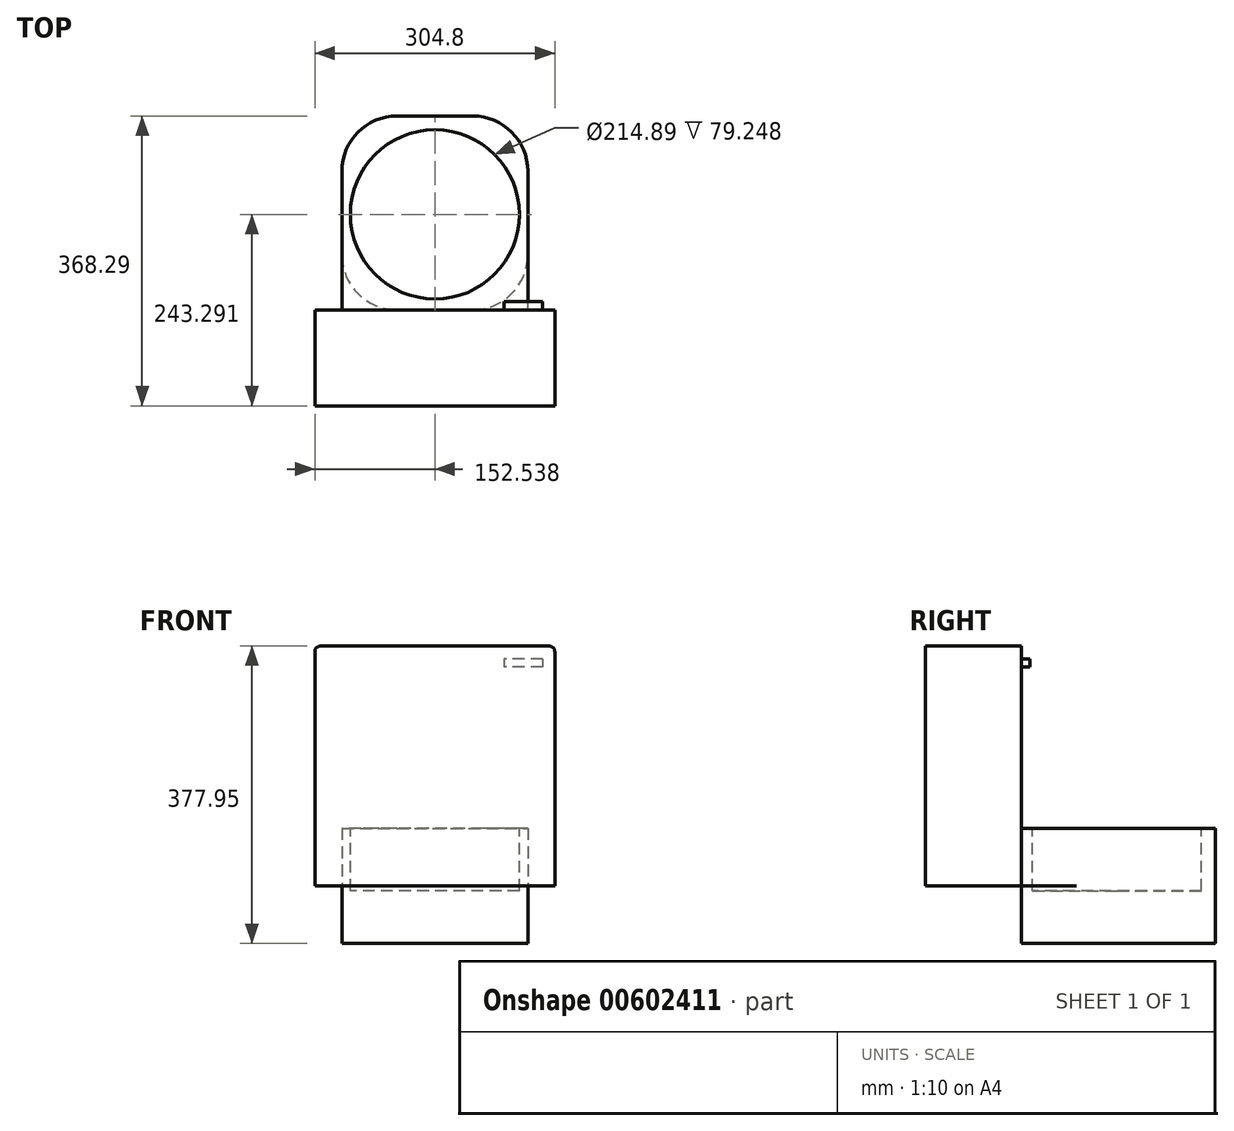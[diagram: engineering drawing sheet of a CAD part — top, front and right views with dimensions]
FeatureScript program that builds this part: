
annotation { "Feature Type Name" : "Feature", "Feature Type Description" : "" }
export const myFeature = defineFeature(function(context is Context, id is Id, definition is map)
    precondition{}
    {
        {
            var Q0;
            Q0=qCreatedBy(makeId("Top.planeOp"),FACE);
            var sketch = newSketch(context, id + "F0", { "sketchPlane" : qUnion([Q0])});
            skLineSegment(sketch, "E0.bottom", {"start": v(0, 0) * mm, "end": v(304.8, 0) * mm});
            skLineSegment(sketch, "E0.top", {"start": v(0, -121.92) * mm, "end": v(304.8, -121.92) * mm});
            skLineSegment(sketch, "E0.left", {"start": v(0, 0) * mm, "end": v(0, -121.92) * mm});
            skLineSegment(sketch, "E0.right", {"start": v(304.8, 0) * mm, "end": v(304.8, -121.92) * mm});
            skSolve(sketch);
        }
        {
            var Q0;
            Q0=makeQuery(id+"F0.imprint","IMPRINT",FACE,{"disambiguationData":[TD([[makeQuery(id+"F0.imprint","IMPRINT",EDGE,{"derivedFrom":sQuery(id+"F0.wireOp",EDGE,"E0.bottom")}),-1.0]])]});
            extrude(context, id + "F1", {"entities" : qUnion([Q0]), "depth" : 304.8 * mm, "offsetDistance" : 30.48 * mm});
        }
        {
            var Q0;
            Q0=qCreatedBy(makeId("Top.planeOp"),FACE);
            var sketch = newSketch(context, id + "F2", { "sketchPlane" : qUnion([Q0])});
            skLineSegment(sketch, "E1.bottom", {"start": v(34.53, 0) * mm, "end": v(270.55, 0) * mm});
            skLineSegment(sketch, "E1.top", {"start": v(34.53, 246.37) * mm, "end": v(270.55, 246.37) * mm});
            skLineSegment(sketch, "E1.left", {"start": v(34.53, 0) * mm, "end": v(34.53, 246.37) * mm});
            skLineSegment(sketch, "E1.right", {"start": v(270.55, 0) * mm, "end": v(270.55, 246.37) * mm});
            skSolve(sketch);
        }
        {
            var Q0;
            Q0=makeQuery(id+"F2.imprint","IMPRINT",FACE,{"disambiguationData":[TD([[makeQuery(id+"F2.imprint","IMPRINT",EDGE,{"derivedFrom":sQuery(id+"F2.wireOp",EDGE,"E1.bottom")}),1.0]])]});
            extrude(context, id + "F3", {"entities" : qUnion([Q0]), "operationType" : NewBodyOperationType.ADD, "endBound" : BoundingType.SYMMETRIC, "depth" : 146.3 * mm, "offsetDistance" : 30.48 * mm});
        }
        {
            var Q0;
            Q0=makeQuery(id+"F3.opExtrude","SWEPT_EDGE",EDGE,{"disambiguationData":[OSD([sQuery(id+"F2.wireOp",EDGE,"E1.top"),sQuery(id+"F2.wireOp",EDGE,"E1.left")])]});
            var Q1;
            Q1=makeQuery(id+"F3.opExtrude","SWEPT_EDGE",EDGE,{"disambiguationData":[OSD([sQuery(id+"F2.wireOp",EDGE,"E1.top"),sQuery(id+"F2.wireOp",EDGE,"E1.right")])]});
            var Q2;
            {var subQ0=sQuery(id+"F2.wireOp",EDGE,"E1.bottom");var subQ1=sQuery(id+"F2.wireOp",EDGE,"E1.left");Q2=makeQuery(id+"F3.boolean.opBoolean","SPLIT",EDGE,{"disambiguationData":[topologyDisambiguationEdgeConnected([makeQuery(id+"F3.opExtrude","SWEPT_FACE",FACE,{"disambiguationData":[OSD([subQ0])]})])],"derivedFrom":makeQuery(id+"F3.opExtrude","SWEPT_EDGE",EDGE,{"disambiguationData":[OSD([subQ0,subQ1])]})});}
            var Q3;
            {var subQ0=sQuery(id+"F2.wireOp",EDGE,"E1.bottom");var subQ1=sQuery(id+"F2.wireOp",EDGE,"E1.right");Q3=makeQuery(id+"F3.boolean.opBoolean","SPLIT",EDGE,{"disambiguationData":[topologyDisambiguationEdgeConnected([makeQuery(id+"F3.opExtrude","SWEPT_FACE",FACE,{"disambiguationData":[OSD([subQ0])]})])],"derivedFrom":makeQuery(id+"F3.opExtrude","SWEPT_EDGE",EDGE,{"disambiguationData":[OSD([subQ0,subQ1])]})});}
            fillet(context, id + "F4", {"entities" : qUnion([Q0, Q1, Q2, Q3]), "radius" : 69.9 * mm, "tangentPropagation" : true, "allowEdgeOverflow" : false});
        }
        {
            var Q0;
            Q0=makeQuery(id+"F3.opExtrude","CAP_FACE",FACE,{"disambiguationData":[OSD([sQuery(id+"F2.wireOp",EDGE,"E1.bottom"),sQuery(id+"F2.wireOp",EDGE,"E1.top"),sQuery(id+"F2.wireOp",EDGE,"E1.left"),sQuery(id+"F2.wireOp",EDGE,"E1.right")])],"isStart":false});
            var sketch = newSketch(context, id + "F5", { "sketchPlane" : qUnion([Q0])});
            skCircle(sketch, "E2", {"center": v(152.54, 121.37) * mm, "radius": 107.45 * mm});
            skPoint(sketch, "E2.centerSnap0", {"position": v(152.54, 246.37) * mm});
            skSolve(sketch);
        }
        {
            var Q0;
            Q0=makeQuery(id+"F5.imprint","IMPRINT",FACE,{"disambiguationData":[TD([[makeQuery(id+"F5.imprint","IMPRINT",EDGE,{"derivedFrom":sQuery(id+"F5.wireOp",EDGE,"E2")}),1.0]])]});
            extrude(context, id + "F6", {"entities" : qUnion([Q0]), "operationType" : NewBodyOperationType.REMOVE, "oppositeDirection" : true, "depth" : 79.25 * mm, "offsetDistance" : 30.48 * mm});
        }
        {
            var Q0;
            Q0=makeQuery(id+"F1.opExtrude","CAP_EDGE",EDGE,{"disambiguationData":[OSD([sQuery(id+"F0.wireOp",EDGE,"E0.right")])],"isStart":false});
            var Q1;
            Q1=makeQuery(id+"F1.opExtrude","CAP_EDGE",EDGE,{"disambiguationData":[OSD([sQuery(id+"F0.wireOp",EDGE,"E0.left")])],"isStart":false});
            fillet(context, id + "F7", {"entities" : qUnion([Q0, Q1]), "radius" : 7.36 * mm, "tangentPropagation" : true, "allowEdgeOverflow" : false});
        }
        {
            var Q0;
            Q0=makeQuery(id+"F1.opExtrude","SWEPT_FACE",FACE,{"disambiguationData":[OSD([sQuery(id+"F0.wireOp",EDGE,"E0.bottom")])]});
            var sketch = newSketch(context, id + "F8", { "sketchPlane" : qUnion([Q0])});
            skLineSegment(sketch, "E3.bottom", {"start": v(-289.43, 288.58) * mm, "end": v(-240.48, 288.58) * mm});
            skLineSegment(sketch, "E3.top", {"start": v(-289.43, 278.45) * mm, "end": v(-240.48, 278.45) * mm});
            skLineSegment(sketch, "E3.left", {"start": v(-289.43, 288.58) * mm, "end": v(-289.43, 278.45) * mm});
            skLineSegment(sketch, "E3.right", {"start": v(-240.48, 288.58) * mm, "end": v(-240.48, 278.45) * mm});
            skSolve(sketch);
        }
        {
            var Q0;
            Q0=makeQuery(id+"F8.imprint","IMPRINT",FACE,{"disambiguationData":[TD([[makeQuery(id+"F8.imprint","IMPRINT",EDGE,{"derivedFrom":sQuery(id+"F8.wireOp",EDGE,"E3.bottom")}),-1.0]])]});
            extrude(context, id + "F9", {"entities" : qUnion([Q0]), "operationType" : NewBodyOperationType.ADD, "depth" : 10.67 * mm, "offsetDistance" : 30.48 * mm});
        }
    });
